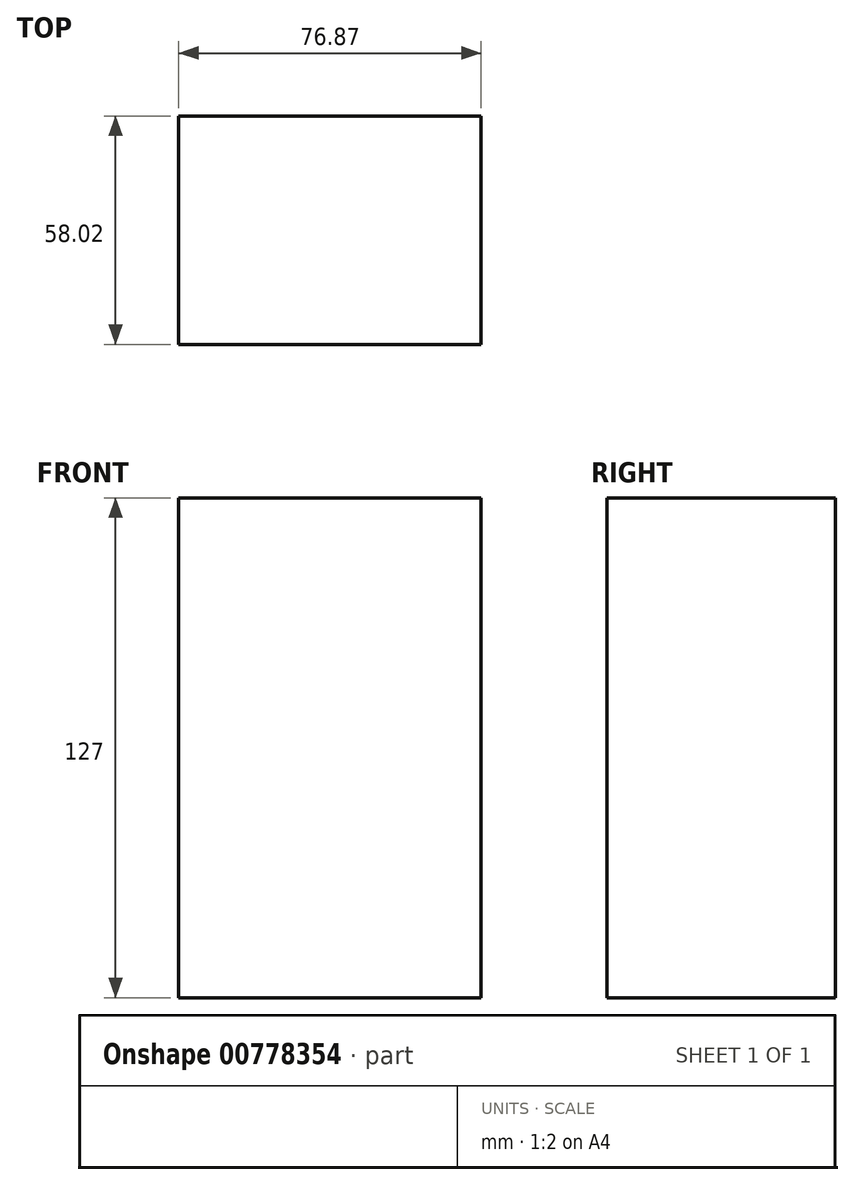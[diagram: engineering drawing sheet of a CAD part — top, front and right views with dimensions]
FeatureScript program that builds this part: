
annotation { "Feature Type Name" : "Feature", "Feature Type Description" : "" }
export const myFeature = defineFeature(function(context is Context, id is Id, definition is map)
    precondition{}
    {
        {
            var Q0;
            Q0=qCreatedBy(makeId("Top.planeOp"),FACE);
            var sketch = newSketch(context, id + "F0", { "sketchPlane" : qUnion([Q0])});
            skLineSegment(sketch, "E0.bottom", {"start": v(0, 0) * mm, "end": v(-76.87, 0) * mm});
            skLineSegment(sketch, "E0.top", {"start": v(0, 58.02) * mm, "end": v(-76.87, 58.02) * mm});
            skLineSegment(sketch, "E0.left", {"start": v(0, 0) * mm, "end": v(0, 58.02) * mm});
            skLineSegment(sketch, "E0.right", {"start": v(-76.87, 0) * mm, "end": v(-76.87, 58.02) * mm});
            skSolve(sketch);
        }
        {
            var Q0;
            Q0 = qSketchRegion(id + "F0", true);
            extrude(context, id + "F1", {"entities" : qUnion([Q0]), "depth" : 127 * mm, "offsetDistance" : 25.4 * mm});
        }
    });
